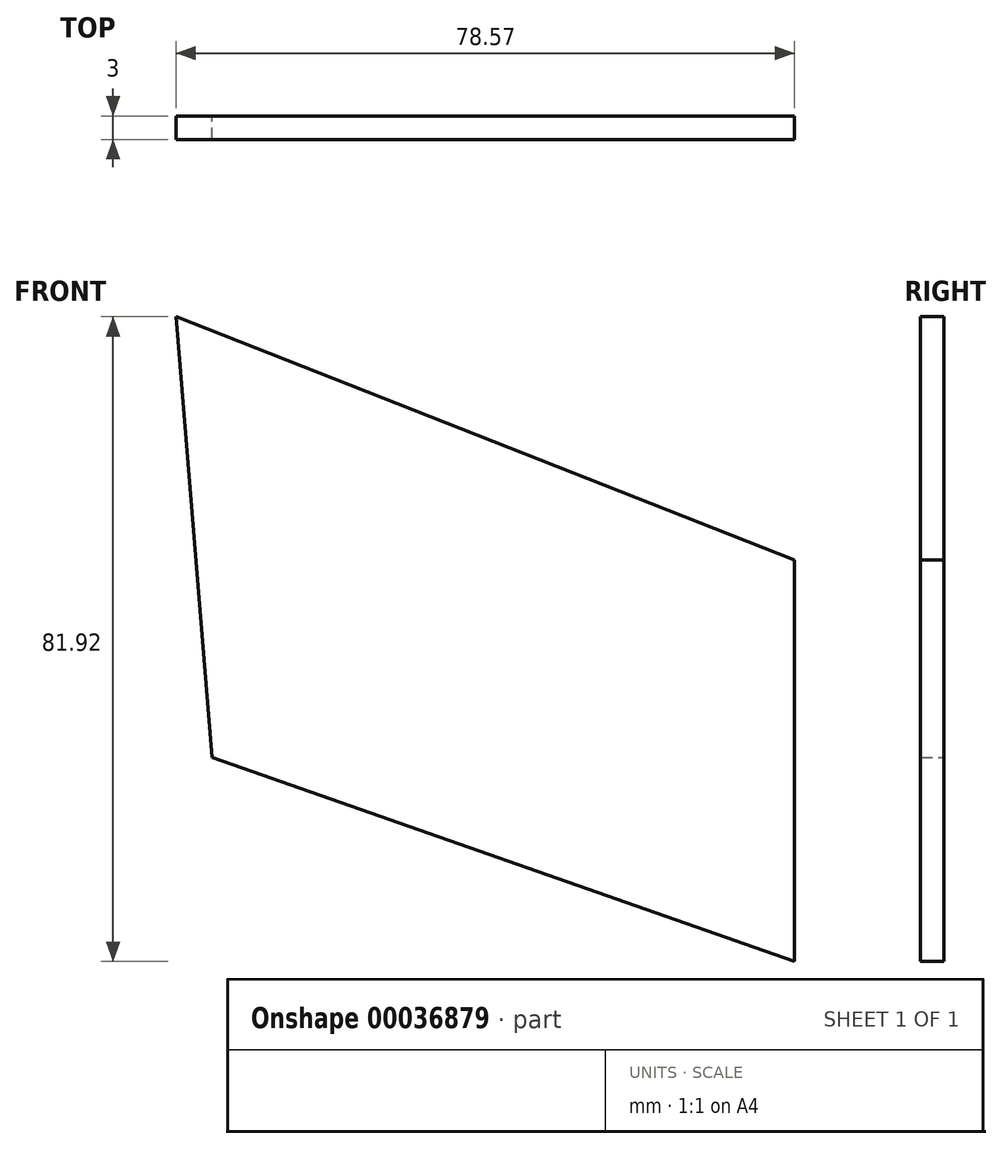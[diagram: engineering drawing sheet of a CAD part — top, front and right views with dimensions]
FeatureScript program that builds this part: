
annotation { "Feature Type Name" : "Feature", "Feature Type Description" : "" }
export const myFeature = defineFeature(function(context is Context, id is Id, definition is map)
    precondition{}
    {
        {
            var Q0;
            Q0=qCreatedBy(makeId("Front.planeOp"),FACE);
            var sketch = newSketch(context, id + "F0", { "sketchPlane" : qUnion([Q0])});
            skLineSegment(sketch, "E0", {"start": v(-56.12, 56) * mm, "end": v(22.45, 25.1) * mm});
            skLineSegment(sketch, "E1", {"start": v(22.45, 25.1) * mm, "end": v(22.45, -25.93) * mm});
            skLineSegment(sketch, "E2", {"start": v(22.45, -25.93) * mm, "end": v(-51.53, 0) * mm});
            skLineSegment(sketch, "E3", {"start": v(-51.53, 0) * mm, "end": v(-56.12, 56) * mm});
            skSolve(sketch);
        }
        {
            var Q0;
            Q0=makeQuery(id+"F0.imprint","IMPRINT",FACE,{"disambiguationData":[TD([[makeQuery(id+"F0.imprint","IMPRINT",EDGE,{"derivedFrom":sQuery(id+"F0.wireOp",EDGE,"E0")}),-1.0]])]});
            extrude(context, id + "F1", {"entities" : qUnion([Q0]), "depth" : 3 * mm});
        }
    });
